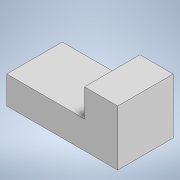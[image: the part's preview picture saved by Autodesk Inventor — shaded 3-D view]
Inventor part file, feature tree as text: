
AUTODESK INVENTOR PART (.ipt)
format: ipt  version: 2022 (Build 260153000, 153)  size: 92,672 bytes
history: native  units: mm
features: other x1, extrude x1, sketch x1
ambient origin geometry x8: Origin, YZ Plane, XZ Plane, XY Plane, X Axis, Y Axis, Z Axis, Center Point
bodies: Body1 (feature_tree)
feature tree (3):
  other  "Sólido1"
  extrude  "Extrusão1"  Depth=30.0mm
  sketch  "Esboço1"  dims[d0=60.0mm d1=30.0mm d2=18.0mm d3=15.0mm d4=42.0mm d5=30.0mm d6=0.0mm]
